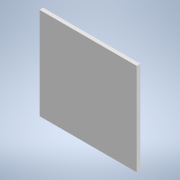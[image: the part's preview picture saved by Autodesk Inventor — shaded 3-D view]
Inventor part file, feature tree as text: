
AUTODESK INVENTOR PART (.ipt)
format: ipt  version: 2020 (Build 240168000, 168)  size: 94,208 bytes
history: native  units: mm
features: other x11, extrude x1, sketch x1
ambient origin geometry x8: Origin, YZ Plane, XZ Plane, XY Plane, X Axis, Y Axis, Z Axis, Center Point
bodies: Body1 (feature_tree)
feature tree (13):
  other  "Sólido1"
  extrude  "Extrusão1"  Depth=3.0mm TaperAngle=0.0deg
  sketch  "Esboço1"  dims[d0=80.0mm d1=3.0mm d2=0.0mm]
  other  "Referência1"
  other  "Referência2"
  other  "Referência3"
  other  "Referência4"
  other  "<userpath>\Desktop\rabo\3d\ela.iam"
  other  "ela.iam"
  other  "PCB:1"
  other  "XL4005_MODELO_3D_1:1"
  other  "basesinha:1"
  other  "Component2:1"
